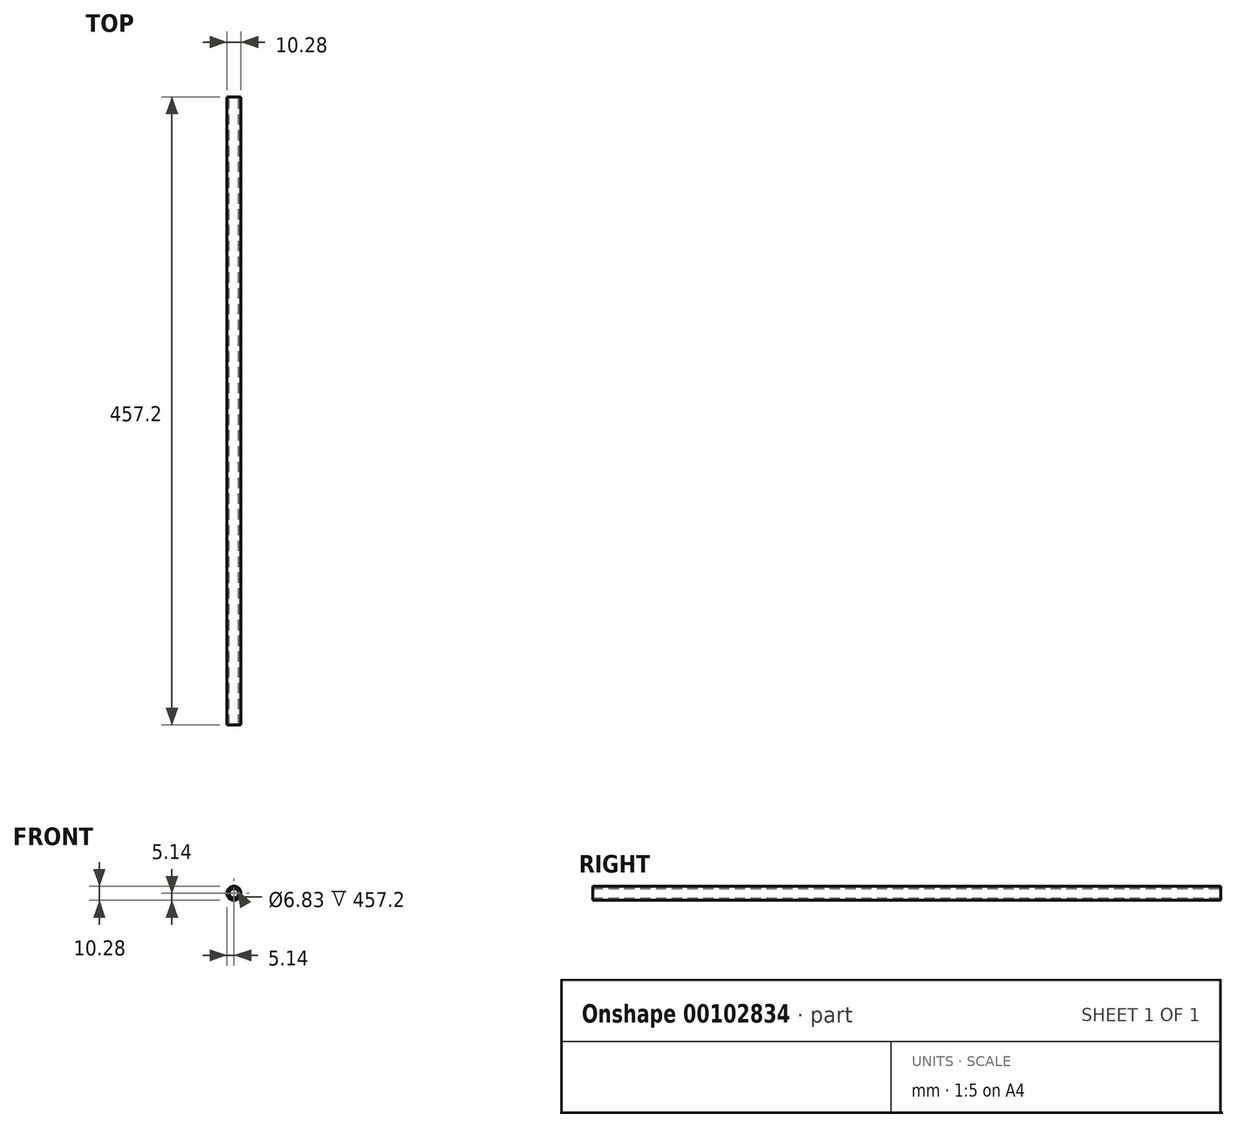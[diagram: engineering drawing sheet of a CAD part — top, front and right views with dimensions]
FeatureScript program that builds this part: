
annotation { "Feature Type Name" : "Feature", "Feature Type Description" : "" }
export const myFeature = defineFeature(function(context is Context, id is Id, definition is map)
    precondition{}
    {
        {
            var Q0;
            Q0=qCreatedBy(makeId("Front.planeOp"),FACE);
            var sketch = newSketch(context, id + "F0", { "sketchPlane" : qUnion([Q0])});
            skCircle(sketch, "E0", {"center": v(0, 0) * mm, "radius": 3.42 * mm});
            skCircle(sketch, "E1", {"center": v(0, 0) * mm, "radius": 5.14 * mm});
            skSolve(sketch);
        }
        {
            var Q0;
            Q0=makeQuery(id+"F0.imprint","IMPRINT",FACE,{"disambiguationData":[TD([[makeQuery(id+"F0.imprint","IMPRINT",EDGE,{"derivedFrom":sQuery(id+"F0.wireOp",EDGE,"E0")}),-1.0]])]});
            extrude(context, id + "F1", {"entities" : qUnion([Q0]), "endBound" : BoundingType.SYMMETRIC, "depth" : 457.2 * mm});
        }
    });
